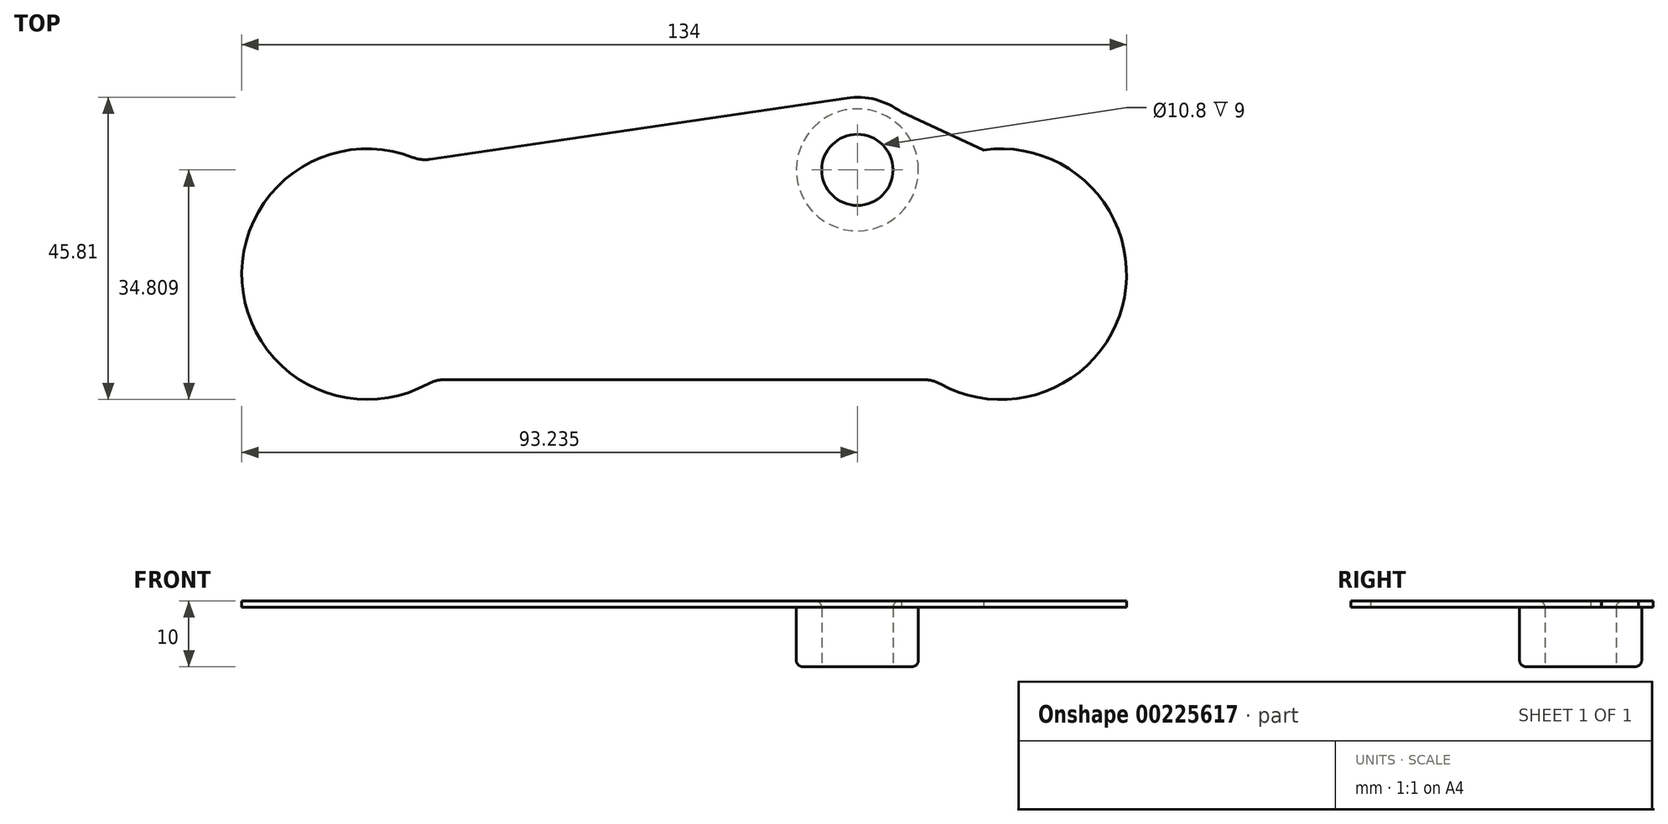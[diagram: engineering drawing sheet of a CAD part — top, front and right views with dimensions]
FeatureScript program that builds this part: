
annotation { "Feature Type Name" : "Feature", "Feature Type Description" : "" }
export const myFeature = defineFeature(function(context is Context, id is Id, definition is map)
    precondition{}
    {
        {
            var Q0;
            Q0=qCreatedBy(makeId("Top.planeOp"),FACE);
            var sketch = newSketch(context, id + "F0", { "sketchPlane" : qUnion([Q0])});
            skLineSegment(sketch, "E0.bottom", {"start": v(0, 0) * mm, "end": v(128, 0) * mm, "construction": true});
            skLineSegment(sketch, "E0.top", {"start": v(0, 32) * mm, "end": v(101.23, 32) * mm, "construction": true});
            skLineSegment(sketch, "E0.left", {"start": v(0, 0) * mm, "end": v(0, 32) * mm, "construction": true});
            skLineSegment(sketch, "E0.right", {"start": v(128, 0) * mm, "end": v(128, 32) * mm, "construction": true});
            skLineSegment(sketch, "E1", {"start": v(0, 16) * mm, "end": v(128, 16) * mm, "construction": true});
            skLineSegment(sketch, "E2", {"start": v(16, 0) * mm, "end": v(16, 32) * mm, "construction": true});
            skLineSegment(sketch, "E3", {"start": v(112, 0) * mm, "end": v(112, 32) * mm, "construction": true});
            skLineSegment(sketch, "E4", {"start": v(27.62, 0) * mm, "end": v(100.38, 0) * mm});
            skCircle(sketch, "E5", {"center": v(90.24, 31.8) * mm, "radius": 5.4 * mm});
            skArc(sketch, "E6", {"start": v(96.9, 40.56) * mm, "mid": v(92.98, 42.46) * mm, "end": v(88.63, 42.7) * mm});
            skCircle(sketch, "E7", {"center": v(112, 16) * mm, "radius": 12.5 * mm, "construction": true});
            skCircle(sketch, "E8", {"center": v(16, 16) * mm, "radius": 12.5 * mm, "construction": true});
            skLineSegment(sketch, "E9", {"start": v(90.24, 31.8) * mm, "end": v(90.24, 42.8) * mm, "construction": true});
            skLineSegment(sketch, "E10", {"start": v(90.24, 31.8) * mm, "end": v(90.24, 20.8) * mm, "construction": true});
            skLineSegment(sketch, "E11", {"start": v(90.24, 31.8) * mm, "end": v(98.01, 39.59) * mm, "construction": true});
            skLineSegment(sketch, "E12", {"start": v(112, 16) * mm, "end": v(123.31, 27.31) * mm, "construction": true});
            skLineSegment(sketch, "E13", {"start": v(112, 16) * mm, "end": v(100.69, 4.69) * mm, "construction": true});
            skLineSegment(sketch, "E14", {"start": v(96.9, 40.56) * mm, "end": v(109.38, 34.82) * mm});
            skLineSegment(sketch, "E15", {"start": v(25.49, 33.4) * mm, "end": v(88.63, 42.7) * mm});
            skLineSegment(sketch, "E16.trimOffspring", {"start": v(112, 32) * mm, "end": v(128, 32) * mm, "construction": true});
            skArc(sketch, "E17.1", {"start": v(102.8, -0.62) * mm, "mid": v(130.68, 12.53) * mm, "end": v(109.38, 34.82) * mm});
            skArc(sketch, "E18.0", {"start": v(22.94, 33.69) * mm, "mid": v(-2.96, 14.75) * mm, "end": v(25.2, -0.63) * mm});
            skLineSegment(sketch, "E19.trimOffspring", {"start": v(90.43, 32) * mm, "end": v(90.24, 32) * mm});
            skLineSegment(sketch, "E20.trimOffspring", {"start": v(109.33, 0.22) * mm, "end": v(109.26, 0) * mm});
            skPoint(sketch, "E21.visualSharp", {"position": v(24.1, 33.2) * mm});
            skArc(sketch, "E21.filletArc", {"start": v(22.94, 33.69) * mm, "mid": v(24.2, 33.38) * mm, "end": v(25.49, 33.4) * mm});
            skPoint(sketch, "E22.visualSharp", {"position": v(26.25, 0) * mm});
            skArc(sketch, "E22.filletArc", {"start": v(27.62, 0) * mm, "mid": v(26.37, -0.16) * mm, "end": v(25.2, -0.63) * mm});
            skArc(sketch, "E23.filletArc", {"start": v(102.8, -0.63) * mm, "mid": v(101.63, -0.16) * mm, "end": v(100.38, 0) * mm});
            skSolve(sketch);
        }
        {
            var Q0;
            Q0 = qSketchRegion(id + "F0", true);
            extrude(context, id + "F1", {"entities" : qUnion([Q0]), "depth" : 1 * mm});
        }
        {
            var Q0;
            Q0=makeQuery(id+"F1.opExtrude","CAP_FACE",FACE,{"disambiguationData":[OSD([sQuery(id+"F0.wireOp",EDGE,"56cc264c-6541-49fd-92ea-d37f6fbfb37f"),sQuery(id+"F0.wireOp",EDGE,"63b3a52b-944e-436c-abaa-7e2b15dfe899"),sQuery(id+"F0.wireOp",EDGE,"E4"),sQuery(id+"F0.wireOp",EDGE,"E5"),sQuery(id+"F0.wireOp",EDGE,"E6"),sQuery(id+"F0.wireOp",EDGE,"E14"),sQuery(id+"F0.wireOp",EDGE,"E15")])],"isStart":true});
            var sketch = newSketch(context, id + "F2", { "sketchPlane" : qUnion([Q0])});
            skCircle(sketch, "E24", {"center": v(90.24, -31.8) * mm, "radius": 9.25 * mm});
            skCircle(sketch, "E25", {"center": v(90.24, -31.8) * mm, "radius": 5.22 * mm});
            skSolve(sketch);
        }
        {
            var Q0;
            Q0=makeQuery(id+"F2.imprint","IMPRINT",FACE,{"disambiguationData":[TD([[makeQuery(id+"F2.imprint","IMPRINT",EDGE,{"derivedFrom":sQuery(id+"F2.wireOp",EDGE,"E24")}),1.0]])]});
            extrude(context, id + "F3", {"entities" : qUnion([Q0]), "operationType" : NewBodyOperationType.ADD, "depth" : 9 * mm});
        }
        {
            var Q0;
            Q0=makeQuery(id+"F3.opExtrude","CAP_EDGE",EDGE,{"disambiguationData":[OSD([sQuery(id+"F2.wireOp",EDGE,"E24")])],"isStart":false});
            var Q1;
            Q1=makeQuery(id+"F1.opExtrude","CAP_EDGE",EDGE,{"disambiguationData":[OSD([sQuery(id+"F0.wireOp",EDGE,"E5")])],"isStart":false});
            fillet(context, id + "F4", {"entities" : qUnion([Q0, Q1]), "radius" : 1 * mm, "tangentPropagation" : true, "allowEdgeOverflow" : false});
        }
    });
